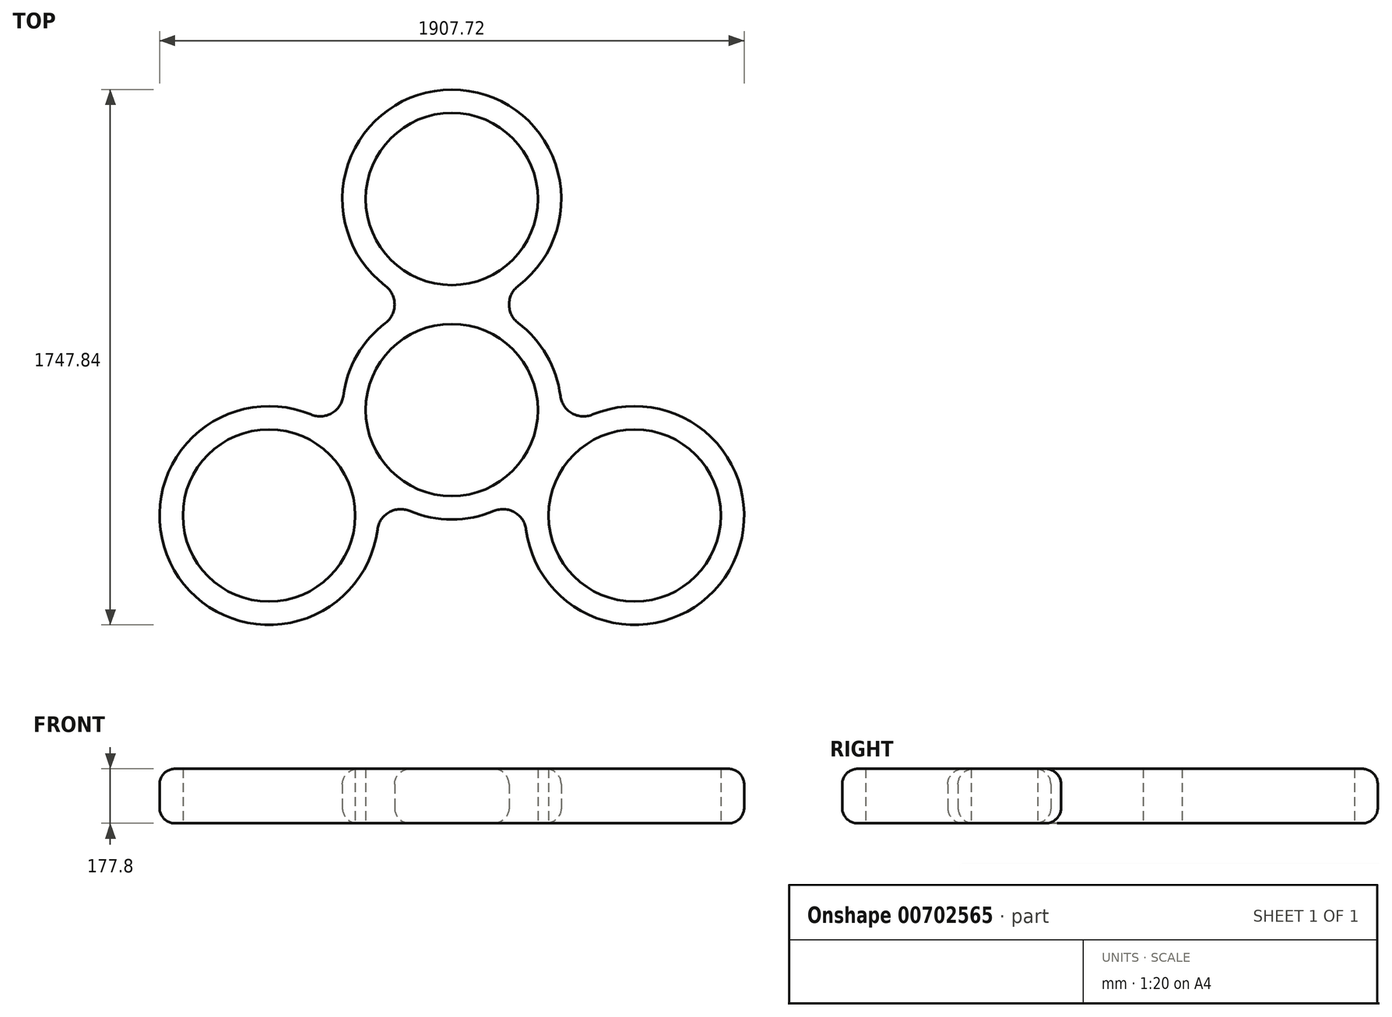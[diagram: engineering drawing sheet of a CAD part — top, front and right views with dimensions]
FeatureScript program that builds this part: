
annotation { "Feature Type Name" : "Feature", "Feature Type Description" : "" }
export const myFeature = defineFeature(function(context is Context, id is Id, definition is map)
    precondition{}
    {
        {
            var Q0;
            Q0=qCreatedBy(makeId("Top.planeOp"),FACE);
            var sketch = newSketch(context, id + "F0", { "sketchPlane" : qUnion([Q0])});
            skCircle(sketch, "E0", {"center": v(0, 0) * mm, "radius": 280.99 * mm});
            skLineSegment(sketch, "E1", {"start": v(0, 0) * mm, "end": v(0, 688.98) * mm});
            skCircle(sketch, "E2", {"center": v(0, 688.98) * mm, "radius": 280.99 * mm});
            skCircle(sketch, "E3.1.0", {"center": v(-596.67, -344.49) * mm, "radius": 280.99 * mm});
            skCircle(sketch, "E3.2.0", {"center": v(596.67, -344.49) * mm, "radius": 280.99 * mm});
            skArc(sketch, "E4", {"start": v(-216.73, 283.92) * mm, "mid": v(-309.33, 178.6) * mm, "end": v(-354.25, 45.74) * mm});
            skArc(sketch, "E5", {"start": v(216.73, 405.06) * mm, "mid": v(0, 1046.16) * mm, "end": v(-216.73, 405.06) * mm});
            skArc(sketch, "E6", {"start": v(-459.16, -14.83) * mm, "mid": v(-906, -523.08) * mm, "end": v(-242.42, -390.22) * mm});
            skLineSegment(sketch, "E7", {"start": v(-251.14, -254) * mm, "end": v(-251.14, -254) * mm});
            skLineSegment(sketch, "E8", {"start": v(-345.53, -90.5) * mm, "end": v(-345.53, -90.5) * mm});
            skArc(sketch, "E9", {"start": v(242.42, -390.22) * mm, "mid": v(906, -523.08) * mm, "end": v(459.16, -14.83) * mm});
            skLineSegment(sketch, "E10", {"start": v(345.53, -90.5) * mm, "end": v(345.53, -90.5) * mm});
            skArc(sketch, "E11", {"start": v(354.25, 45.74) * mm, "mid": v(309.33, 178.6) * mm, "end": v(216.73, 283.92) * mm});
            skArc(sketch, "E12", {"start": v(-137.51, -329.66) * mm, "mid": v(0, -357.19) * mm, "end": v(137.51, -329.66) * mm});
            skPoint(sketch, "E13.visualSharp", {"position": v(-345.53, -90.5) * mm});
            skArc(sketch, "E13.filletArc", {"start": v(-459.16, -14.83) * mm, "mid": v(-391.72, -10.5) * mm, "end": v(-354.25, 45.74) * mm});
            skPoint(sketch, "E14.visualSharp", {"position": v(-251.14, -254) * mm});
            skArc(sketch, "E14.filletArc", {"start": v(-137.51, -329.66) * mm, "mid": v(-204.95, -334) * mm, "end": v(-242.42, -390.22) * mm});
            skPoint(sketch, "E15.visualSharp", {"position": v(251.14, -254) * mm});
            skArc(sketch, "E15.filletArc", {"start": v(242.42, -390.22) * mm, "mid": v(204.95, -334) * mm, "end": v(137.51, -329.66) * mm});
            skPoint(sketch, "E16.visualSharp", {"position": v(345.53, -90.5) * mm});
            skArc(sketch, "E16.filletArc", {"start": v(354.25, 45.74) * mm, "mid": v(391.72, -10.5) * mm, "end": v(459.16, -14.83) * mm});
            skPoint(sketch, "E17.visualSharp", {"position": v(94.4, 344.49) * mm});
            skArc(sketch, "E17.filletArc", {"start": v(216.73, 405.06) * mm, "mid": v(186.77, 344.49) * mm, "end": v(216.73, 283.92) * mm});
            skPoint(sketch, "E18.visualSharp", {"position": v(-94.4, 344.49) * mm});
            skArc(sketch, "E18.filletArc", {"start": v(-216.73, 283.92) * mm, "mid": v(-186.77, 344.49) * mm, "end": v(-216.73, 405.06) * mm});
            skSolve(sketch);
        }
        {
            var Q0;
            Q0=makeQuery(id+"F0.imprint","IMPRINT",FACE,{"disambiguationData":[TD([[makeQuery(id+"F0.imprint","IMPRINT",EDGE,{"derivedFrom":sQuery(id+"F0.wireOp",EDGE,"E0")}),-1.0]])]});
            extrude(context, id + "F1", {"entities" : qUnion([Q0]), "depth" : 177.8 * mm, "offsetDistance" : 25.4 * mm});
        }
        {
            var Q0;
            Q0=makeQuery(id+"F1.opExtrude","CAP_EDGE",EDGE,{"disambiguationData":[OSD([sQuery(id+"F0.wireOp",EDGE,"E6")])],"isStart":false});
            var Q1;
            Q1=makeQuery(id+"F1.opExtrude","CAP_EDGE",EDGE,{"disambiguationData":[OSD([sQuery(id+"F0.wireOp",EDGE,"E6")])],"isStart":true});
            fillet(context, id + "F2", {"entities" : qUnion([Q0, Q1]), "radius" : 50.8 * mm, "tangentPropagation" : true, "allowEdgeOverflow" : false});
        }
    });
